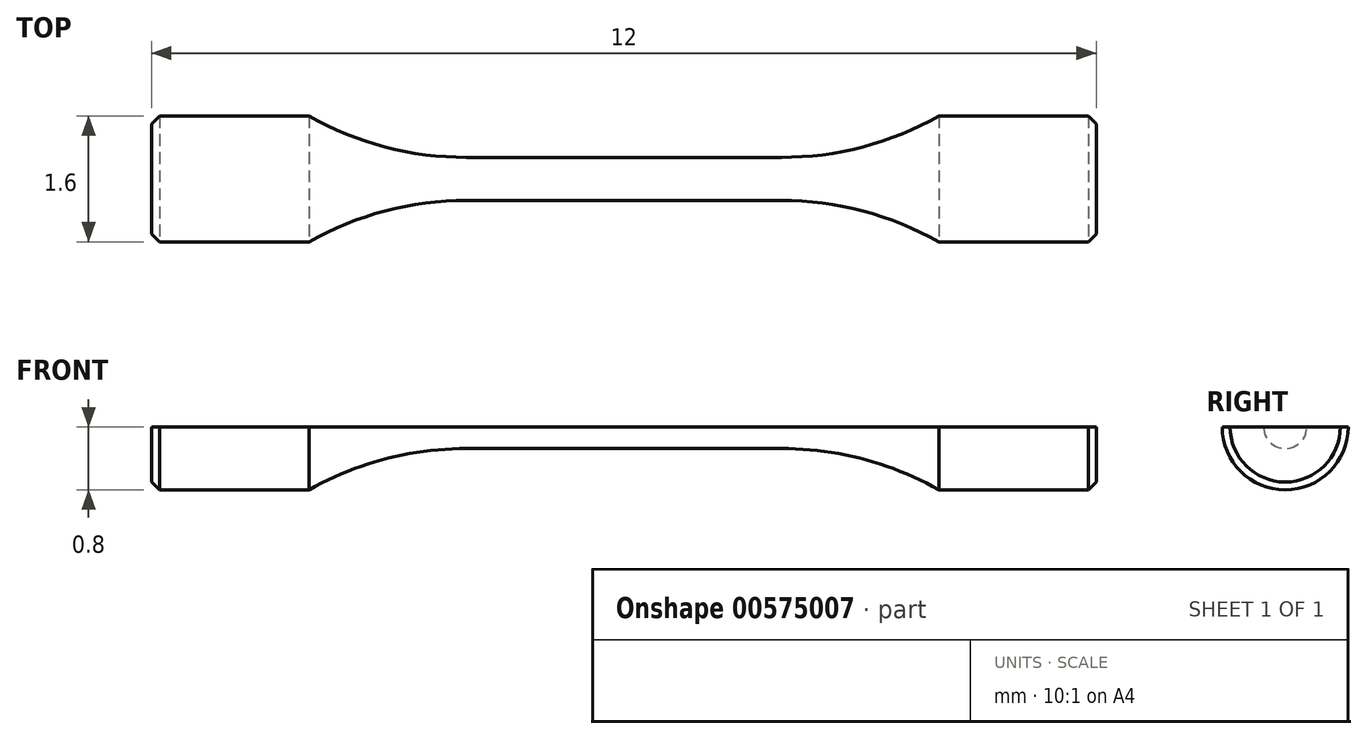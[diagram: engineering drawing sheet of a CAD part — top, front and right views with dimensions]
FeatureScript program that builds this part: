
annotation { "Feature Type Name" : "Feature", "Feature Type Description" : "" }
export const myFeature = defineFeature(function(context is Context, id is Id, definition is map)
    precondition{}
    {
        {
            var Q0;
            Q0=qCreatedBy(makeId("Top.planeOp"),FACE);
            var sketch = newSketch(context, id + "F0", { "sketchPlane" : qUnion([Q0])});
            skLineSegment(sketch, "E0", {"start": v(-6, 0) * mm, "end": v(-6, 0.8) * mm});
            skLineSegment(sketch, "E1", {"start": v(-6, 0.8) * mm, "end": v(-4, 0.8) * mm});
            skLineSegment(sketch, "E2", {"start": v(-2, 0.28) * mm, "end": v(0, 0.28) * mm});
            skLineSegment(sketch, "E3.MirrorCS", {"start": v(6, 0.8) * mm, "end": v(4, 0.8) * mm});
            skLineSegment(sketch, "E4.MirrorCS", {"start": v(6, 0) * mm, "end": v(6, 0.8) * mm});
            skLineSegment(sketch, "E5.MirrorCS", {"start": v(2, 0.28) * mm, "end": v(0, 0.28) * mm});
            skArc(sketch, "E6", {"start": v(-4, 0.8) * mm, "mid": v(-3.03, 0.4) * mm, "end": v(-2, 0.28) * mm});
            skArc(sketch, "E7.MirrorCS", {"start": v(4, 0.8) * mm, "mid": v(3.03, 0.4) * mm, "end": v(2, 0.28) * mm});
            skLineSegment(sketch, "E8", {"start": v(-6, 0) * mm, "end": v(6, 0) * mm});
            skSolve(sketch);
        }
        {
            var Q0;
            Q0=makeQuery(id+"F0.imprint","IMPRINT",FACE,{"disambiguationData":[TD([[makeQuery(id+"F0.imprint","IMPRINT",EDGE,{"derivedFrom":sQuery(id+"F0.wireOp",EDGE,"E0")}),-1.0]])]});
            var Q1;
            Q1=sQuery(id+"F0.wireOp",EDGE,"E8");
            revolve(context, id + "F1", {"surfaceOperationType" : NewSurfaceOperationType.NEW, "entities" : qUnion([Q0]), "axis" : qUnion([Q1]), "revolveType" : RevolveType.FULL});
        }
        {
            var Q0;
            Q0=makeQuery(id+"F1.opRevolve","SWEPT_EDGE",EDGE,{"disambiguationData":[OSD([sQuery(id+"F0.wireOp",EDGE,"E0"),sQuery(id+"F0.wireOp",EDGE,"E1")])]});
            var Q1;
            Q1=makeQuery(id+"F1.opRevolve","SWEPT_EDGE",EDGE,{"disambiguationData":[OSD([sQuery(id+"F0.wireOp",EDGE,"E3.MirrorCS"),sQuery(id+"F0.wireOp",EDGE,"E4.MirrorCS")])]});
            chamfer(context, id + "F2", {"entities" : qUnion([Q0, Q1]), "width" : 0.1 * mm, "tangentPropagation" : true});
        }
        {
            var Q0;
            Q0=makeQuery(id+"F1.opRevolve","SWEPT_FACE",FACE,{"disambiguationData":[OSD([sQuery(id+"F0.wireOp",EDGE,"E0")])]});
            var sketch = newSketch(context, id + "F3", { "sketchPlane" : qUnion([Q0])});
            skLineSegment(sketch, "E9.bottom", {"start": v(0.94, 0) * mm, "end": v(-1.46, 0) * mm});
            skLineSegment(sketch, "E9.top", {"start": v(0.94, 1.12) * mm, "end": v(-1.46, 1.12) * mm});
            skLineSegment(sketch, "E9.left", {"start": v(0.94, 0) * mm, "end": v(0.94, 1.12) * mm});
            skLineSegment(sketch, "E9.right", {"start": v(-1.46, 0) * mm, "end": v(-1.46, 1.12) * mm});
            skSolve(sketch);
        }
        {
            var Q0;
            Q0 = qSketchRegion(id + "F3", true);
            extrude(context, id + "F4", {"entities" : qUnion([Q0]), "operationType" : NewBodyOperationType.REMOVE, "endBound" : BoundingType.THROUGH_ALL, "oppositeDirection" : true, "depth" : 25 * mm, "offsetDistance" : 25 * mm});
        }
    });
